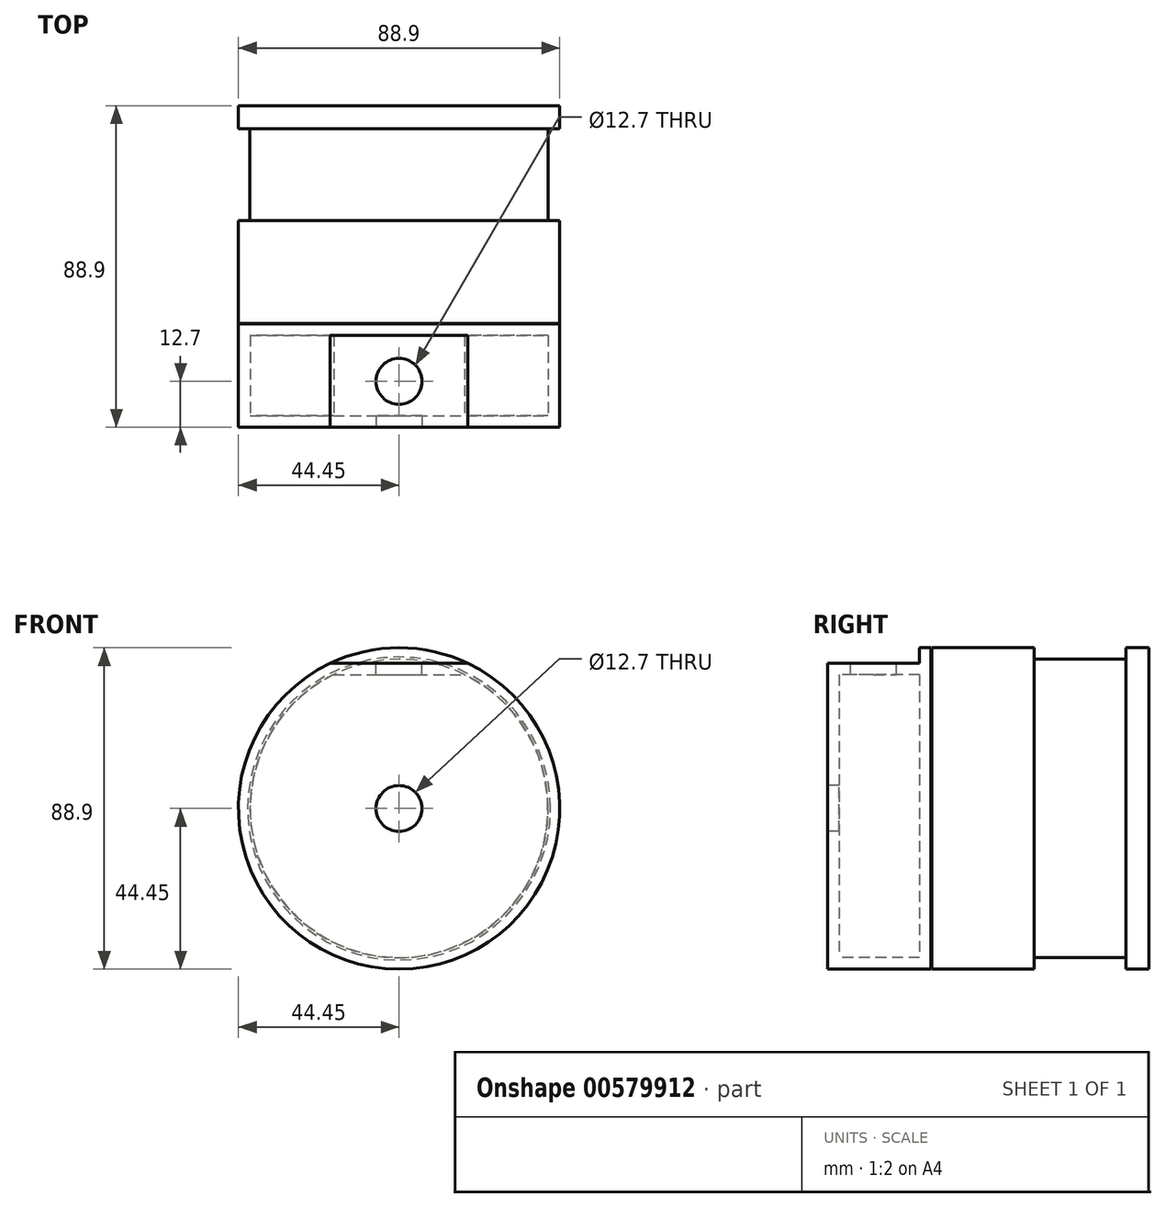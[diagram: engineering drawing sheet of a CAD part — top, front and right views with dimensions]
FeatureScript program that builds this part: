
annotation { "Feature Type Name" : "Feature", "Feature Type Description" : "" }
export const myFeature = defineFeature(function(context is Context, id is Id, definition is map)
    precondition{}
    {
        {
            var Q0;
            Q0=qCreatedBy(makeId("Front.planeOp"),FACE);
            var sketch = newSketch(context, id + "F0", { "sketchPlane" : qUnion([Q0])});
            skCircle(sketch, "E0", {"center": v(0, 0) * mm, "radius": 44.45 * mm});
            skSolve(sketch);
        }
        {
            var Q0;
            Q0 = qSketchRegion(id + "F0", true);
            extrude(context, id + "F1", {"entities" : qUnion([Q0]), "depth" : 88.9 * mm, "offsetDistance" : 25.4 * mm});
        }
        {
            var Q0;
            Q0=makeQuery(id+"F1.opExtrude","CAP_FACE",FACE,{"disambiguationData":[OSD([sQuery(id+"F0.wireOp",EDGE,"E0")])],"isStart":false});
            var sketch = newSketch(context, id + "F2", { "sketchPlane" : qUnion([Q0])});
            skCircle(sketch, "E1", {"center": v(0, 0) * mm, "radius": 6.35 * mm});
            skSolve(sketch);
        }
        {
            var Q0;
            Q0 = qSketchRegion(id + "F2", true);
            extrude(context, id + "F3", {"entities" : qUnion([Q0]), "operationType" : NewBodyOperationType.REMOVE, "oppositeDirection" : true, "depth" : 25.4 * mm, "offsetDistance" : 25.4 * mm});
        }
        {
            var Q0;
            Q0=makeQuery(id+"F1.opExtrude","CAP_FACE",FACE,{"disambiguationData":[OSD([sQuery(id+"F0.wireOp",EDGE,"E0")])],"isStart":false});
            var sketch = newSketch(context, id + "F4", { "sketchPlane" : qUnion([Q0])});
            skLineSegment(sketch, "E2", {"start": v(-19.05, 40.16) * mm, "end": v(19.05, 40.16) * mm});
            skArc(sketch, "E3", {"start": v(19.05, 40.16) * mm, "mid": v(0, 44.45) * mm, "end": v(-19.05, 40.16) * mm});
            skSolve(sketch);
        }
        {
            var Q0;
            Q0 = qSketchRegion(id + "F4", true);
            extrude(context, id + "F5", {"entities" : qUnion([Q0]), "operationType" : NewBodyOperationType.REMOVE, "oppositeDirection" : true, "depth" : 25.4 * mm, "offsetDistance" : 25.4 * mm});
        }
        {
            var Q0;
            Q0=makeQuery(id+"F5.boolean.opBoolean","COPY",FACE,{"derivedFrom":makeQuery(id+"F5.opExtrude","SWEPT_FACE",FACE,{"disambiguationData":[OSD([sQuery(id+"F4.wireOp",EDGE,"E2")])]})});
            var sketch = newSketch(context, id + "F6", { "sketchPlane" : qUnion([Q0])});
            skCircle(sketch, "E4", {"center": v(0, -76.2) * mm, "radius": 6.35 * mm});
            skSolve(sketch);
        }
        {
            var Q0;
            Q0 = qSketchRegion(id + "F6", true);
            extrude(context, id + "F7", {"entities" : qUnion([Q0]), "operationType" : NewBodyOperationType.REMOVE, "oppositeDirection" : true, "depth" : 25.4 * mm, "offsetDistance" : 25.4 * mm});
        }
        {
            var Q0;
            Q0=makeQuery(id+"F1.opExtrude","CAP_FACE",FACE,{"disambiguationData":[OSD([sQuery(id+"F0.wireOp",EDGE,"E0")])],"isStart":false});
            cPlane(context, id + "F8", {"entities" : qUnion([Q0]), "cplaneType" : CPlaneType.OFFSET, "offset" : 3.17 * mm, "oppositeDirection" : true, "width" : 152.4 * mm, "height" : 152.4 * mm});
        }
        {
            var Q0;
            Q0=qCreatedBy(id+"F8.planeOp",FACE);
            var sketch = newSketch(context, id + "F9", { "sketchPlane" : qUnion([Q0])});
            skLineSegment(sketch, "E5", {"start": v(-18.1, 36.99) * mm, "end": v(18.1, 36.99) * mm});
            skArc(sketch, "E6", {"start": v(-18.1, 36.99) * mm, "mid": v(0, -41.18) * mm, "end": v(18.1, 36.99) * mm});
            skSolve(sketch);
        }
        {
            var Q0;
            Q0 = qSketchRegion(id + "F9", true);
            extrude(context, id + "F10", {"entities" : qUnion([Q0]), "operationType" : NewBodyOperationType.REMOVE, "oppositeDirection" : true, "depth" : 22.22 * mm, "offsetDistance" : 25.4 * mm});
        }
        {
            var Q0;
            Q0=makeQuery(id+"F1.opExtrude","CAP_FACE",FACE,{"disambiguationData":[OSD([sQuery(id+"F0.wireOp",EDGE,"E0")])],"isStart":false});
            cPlane(context, id + "F11", {"entities" : qUnion([Q0]), "cplaneType" : CPlaneType.OFFSET, "offset" : 28.57 * mm, "oppositeDirection" : true, "width" : 152.4 * mm, "height" : 152.4 * mm});
        }
        {
            var Q0;
            Q0=qCreatedBy(id+"F11.planeOp",FACE);
            var sketch = newSketch(context, id + "F12", { "sketchPlane" : qUnion([Q0])});
            skCircle(sketch, "E7", {"center": v(0, 0) * mm, "radius": 44.45 * mm});
            skCircle(sketch, "E8", {"center": v(0, 0) * mm, "radius": 41.91 * mm});
            skSolve(sketch);
        }
        {
            var Q0;
            Q0 = qSketchRegion(id + "F12", true);
            extrude(context, id + "F13", {"entities" : qUnion([Q0]), "operationType" : NewBodyOperationType.REMOVE, "oppositeDirection" : true, "depth" : 0.13 * mm, "offsetDistance" : 25.4 * mm});
        }
        {
            var Q0;
            Q0=qCreatedBy(makeId("Front.planeOp"),FACE);
            cPlane(context, id + "F14", {"entities" : qUnion([Q0]), "cplaneType" : CPlaneType.OFFSET, "offset" : 6.35 * mm, "width" : 152.4 * mm, "height" : 152.4 * mm});
        }
        {
            var Q0;
            Q0=qCreatedBy(id+"F14.planeOp",FACE);
            var sketch = newSketch(context, id + "F15", { "sketchPlane" : qUnion([Q0])});
            skCircle(sketch, "E9", {"center": v(0, 0) * mm, "radius": 48.47 * mm});
            skCircle(sketch, "E10", {"center": v(0, 0) * mm, "radius": 41.28 * mm});
            skSolve(sketch);
        }
        {
            var Q0;
            Q0 = qSketchRegion(id + "F15", true);
            extrude(context, id + "F16", {"entities" : qUnion([Q0]), "operationType" : NewBodyOperationType.REMOVE, "depth" : 25.4 * mm, "offsetDistance" : 25.4 * mm});
        }
    });
